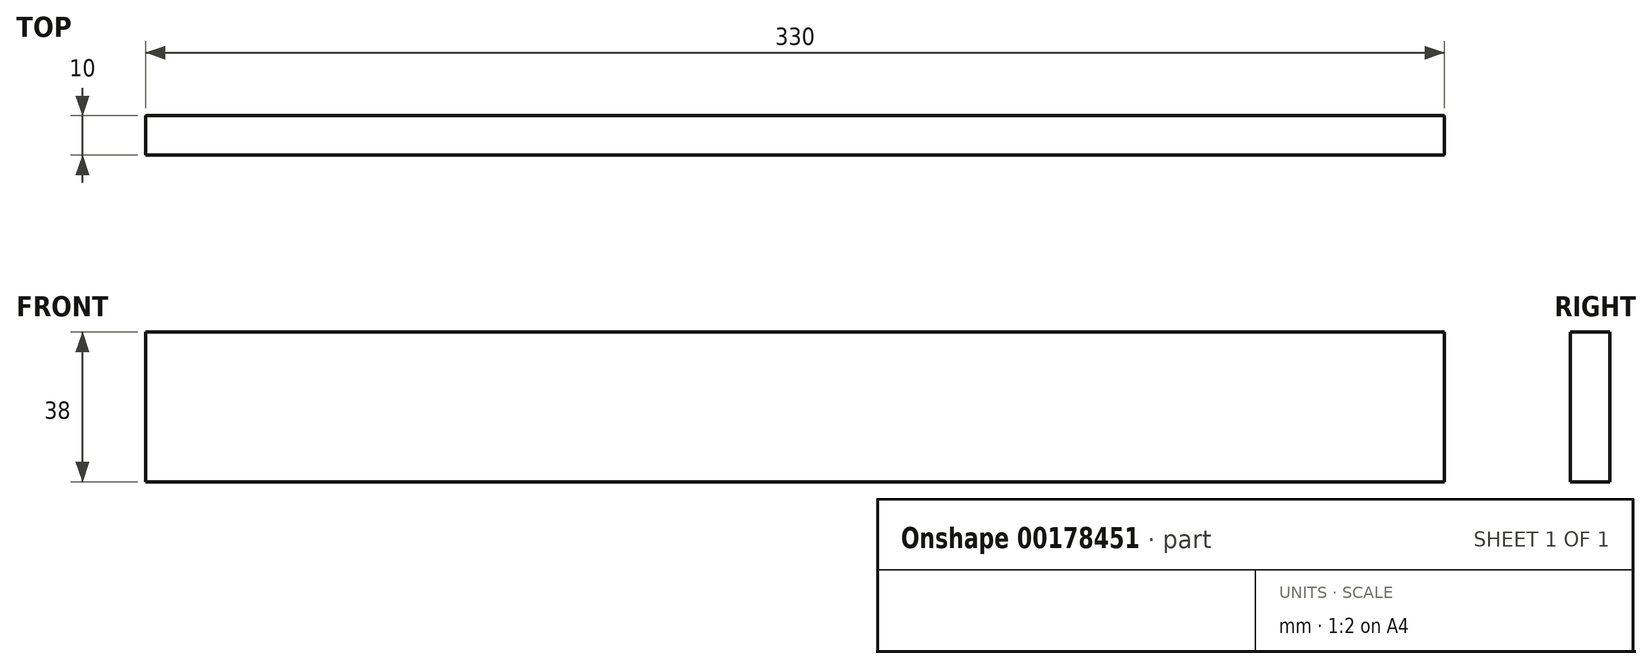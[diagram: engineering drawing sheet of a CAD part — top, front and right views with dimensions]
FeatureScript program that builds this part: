
annotation { "Feature Type Name" : "Feature", "Feature Type Description" : "" }
export const myFeature = defineFeature(function(context is Context, id is Id, definition is map)
    precondition{}
    {
        {
            var Q0;
            Q0=qCreatedBy(makeId("Front.planeOp"),FACE);
            var sketch = newSketch(context, id + "F0", { "sketchPlane" : qUnion([Q0])});
            skLineSegment(sketch, "E0.bottom", {"start": v(0, 0) * mm, "end": v(330, 0) * mm});
            skLineSegment(sketch, "E0.top", {"start": v(0, 38) * mm, "end": v(330, 38) * mm});
            skLineSegment(sketch, "E0.left", {"start": v(0, 0) * mm, "end": v(0, 38) * mm});
            skLineSegment(sketch, "E0.right", {"start": v(330, 0) * mm, "end": v(330, 38) * mm});
            skSolve(sketch);
        }
        {
            var Q0;
            Q0 = qSketchRegion(id + "F0", true);
            extrude(context, id + "F1", {"entities" : qUnion([Q0]), "depth" : 10 * mm});
        }
    });
